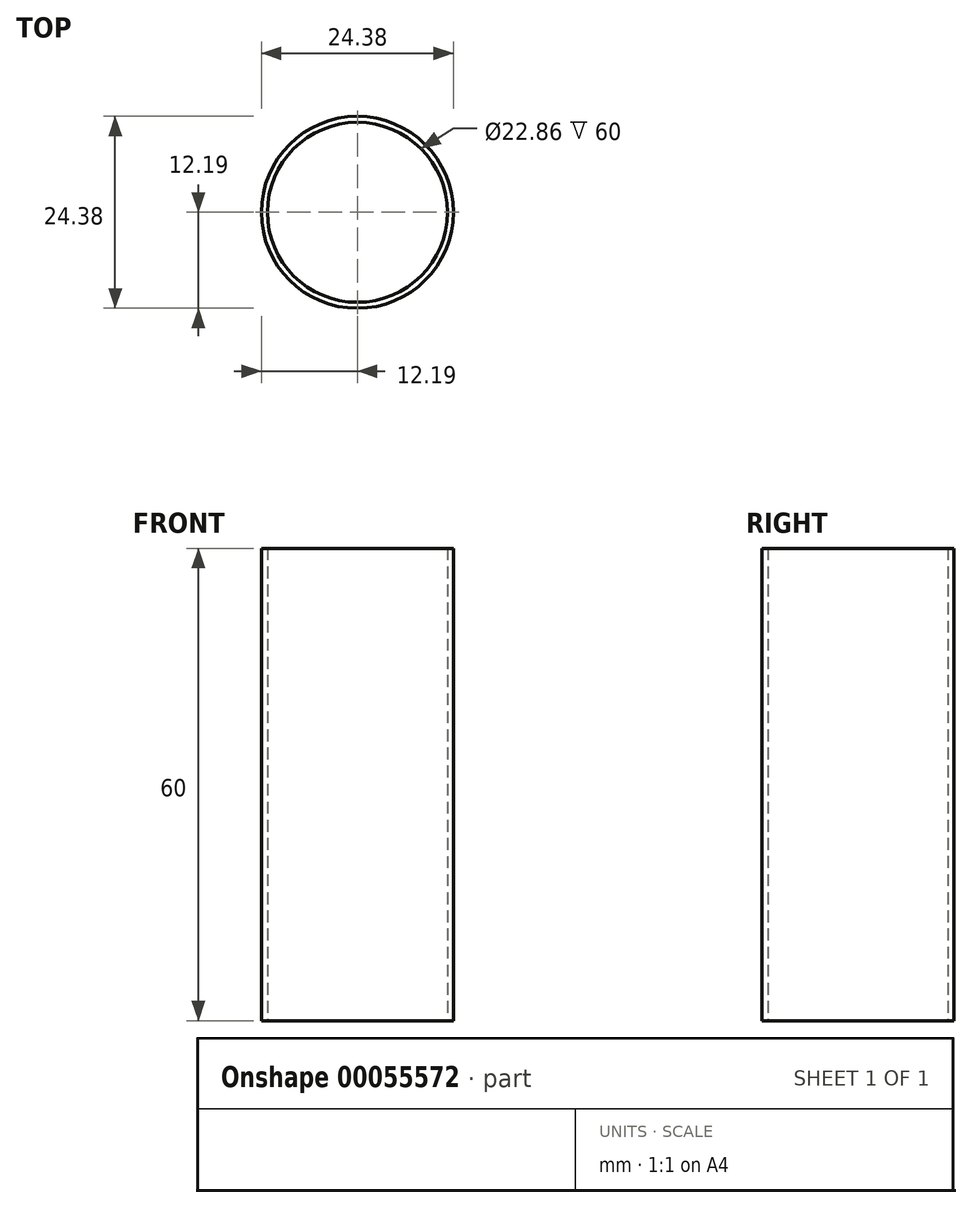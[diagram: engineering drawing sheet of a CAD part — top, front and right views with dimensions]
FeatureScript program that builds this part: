
annotation { "Feature Type Name" : "Feature", "Feature Type Description" : "" }
export const myFeature = defineFeature(function(context is Context, id is Id, definition is map)
    precondition{}
    {
        {
            var Q0;
            Q0=qCreatedBy(makeId("Top.planeOp"),FACE);
            var sketch = newSketch(context, id + "F0", { "sketchPlane" : qUnion([Q0])});
            skCircle(sketch, "E0", {"center": v(0, 0) * mm, "radius": 11.43 * mm});
            skCircle(sketch, "E1", {"center": v(0, 0) * mm, "radius": 12.2 * mm});
            skSolve(sketch);
        }
        {
            var Q0;
            Q0=makeQuery(id+"F0.imprint","IMPRINT",FACE,{"disambiguationData":[TD([[makeQuery(id+"F0.imprint","IMPRINT",EDGE,{"derivedFrom":sQuery(id+"F0.wireOp",EDGE,"E0")}),-1.0]])]});
            extrude(context, id + "F1", {"entities" : qUnion([Q0]), "depth" : 60 * mm});
        }
    });
